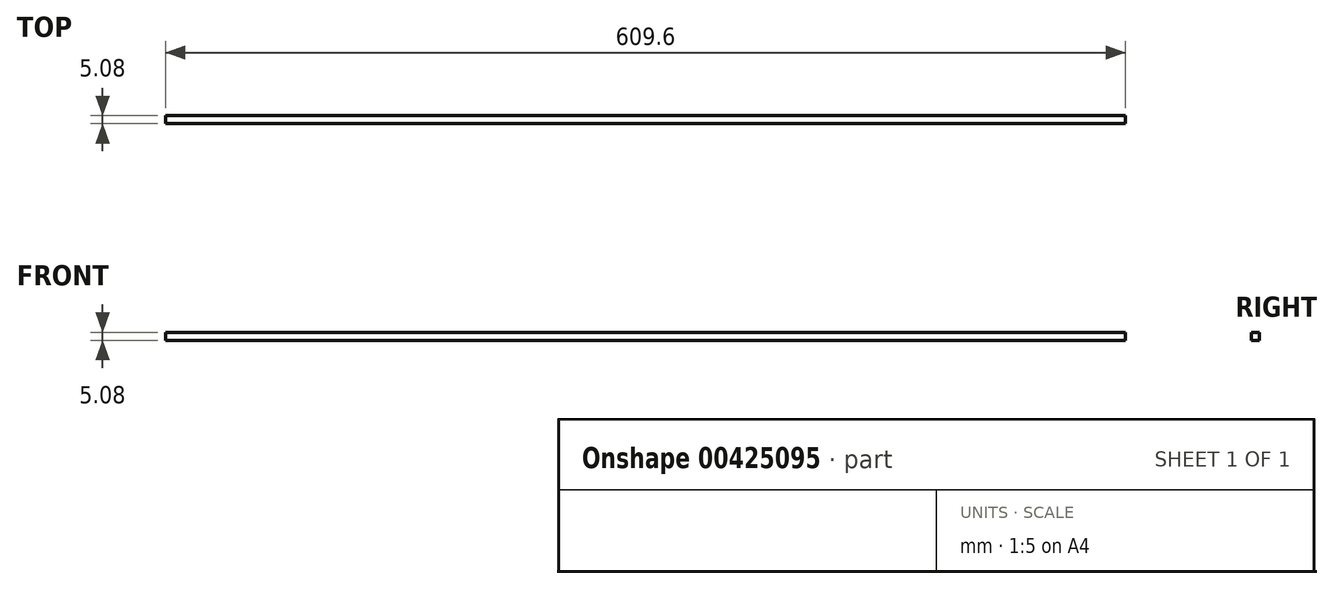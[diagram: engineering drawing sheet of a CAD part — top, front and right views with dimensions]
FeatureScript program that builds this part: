
annotation { "Feature Type Name" : "Feature", "Feature Type Description" : "" }
export const myFeature = defineFeature(function(context is Context, id is Id, definition is map)
    precondition{}
    {
        {
            var Q0;
            Q0=qCreatedBy(makeId("Front.planeOp"),FACE);
            var sketch = newSketch(context, id + "F0", { "sketchPlane" : qUnion([Q0])});
            skLineSegment(sketch, "E0.bottom", {"start": v(-320.94, 13.34) * mm, "end": v(288.66, 13.34) * mm});
            skLineSegment(sketch, "E0.top", {"start": v(-320.94, 8.26) * mm, "end": v(288.66, 8.26) * mm});
            skLineSegment(sketch, "E0.left", {"start": v(-320.94, 13.34) * mm, "end": v(-320.94, 8.26) * mm});
            skLineSegment(sketch, "E0.right", {"start": v(288.66, 13.34) * mm, "end": v(288.66, 8.26) * mm});
            skSolve(sketch);
        }
        {
            var Q0;
            Q0=makeQuery(id+"F0.imprint","IMPRINT",FACE,{"disambiguationData":[TD([[makeQuery(id+"F0.imprint","IMPRINT",EDGE,{"derivedFrom":sQuery(id+"F0.wireOp",EDGE,"E0.bottom")}),-1.0]])]});
            extrude(context, id + "F1", {"entities" : qUnion([Q0]), "depth" : 5.08 * mm});
        }
    });
